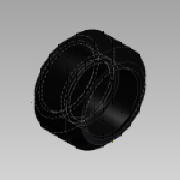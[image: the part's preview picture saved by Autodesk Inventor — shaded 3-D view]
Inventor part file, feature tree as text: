
AUTODESK INVENTOR PART (.ipt)
format: ipt  version: 2013 SP2 (Build 170200200, 200)  size: 136,704 bytes
history: native  units: mm
features: revolve x1, sketch x1
ambient origin geometry x8: Origin, YZ Plane, XZ Plane, XY Plane, X Axis, Y Axis, Z Axis, Center Point
bodies: Solid1 (feature_tree)
feature tree (2):
  revolve  "Revolution1"  [1 undecoded]
  sketch  "Sketch1"  dims[d0=5.0mm d1=20.0mm d2=90.0deg d3=8.64mm d4=15.23mm d5=0.5mm d6=3.9mm d7=12.21mm d8=9.974mm d9=135.0deg d10=0.3mm d11=0.3mm d12=5.78mm d13=90.0deg]
note: 1 required parameter value undecoded (feature->parameter linkage not recoverable at this tier; creation-order binding heuristic only, values carry confidence <= 0.55)
